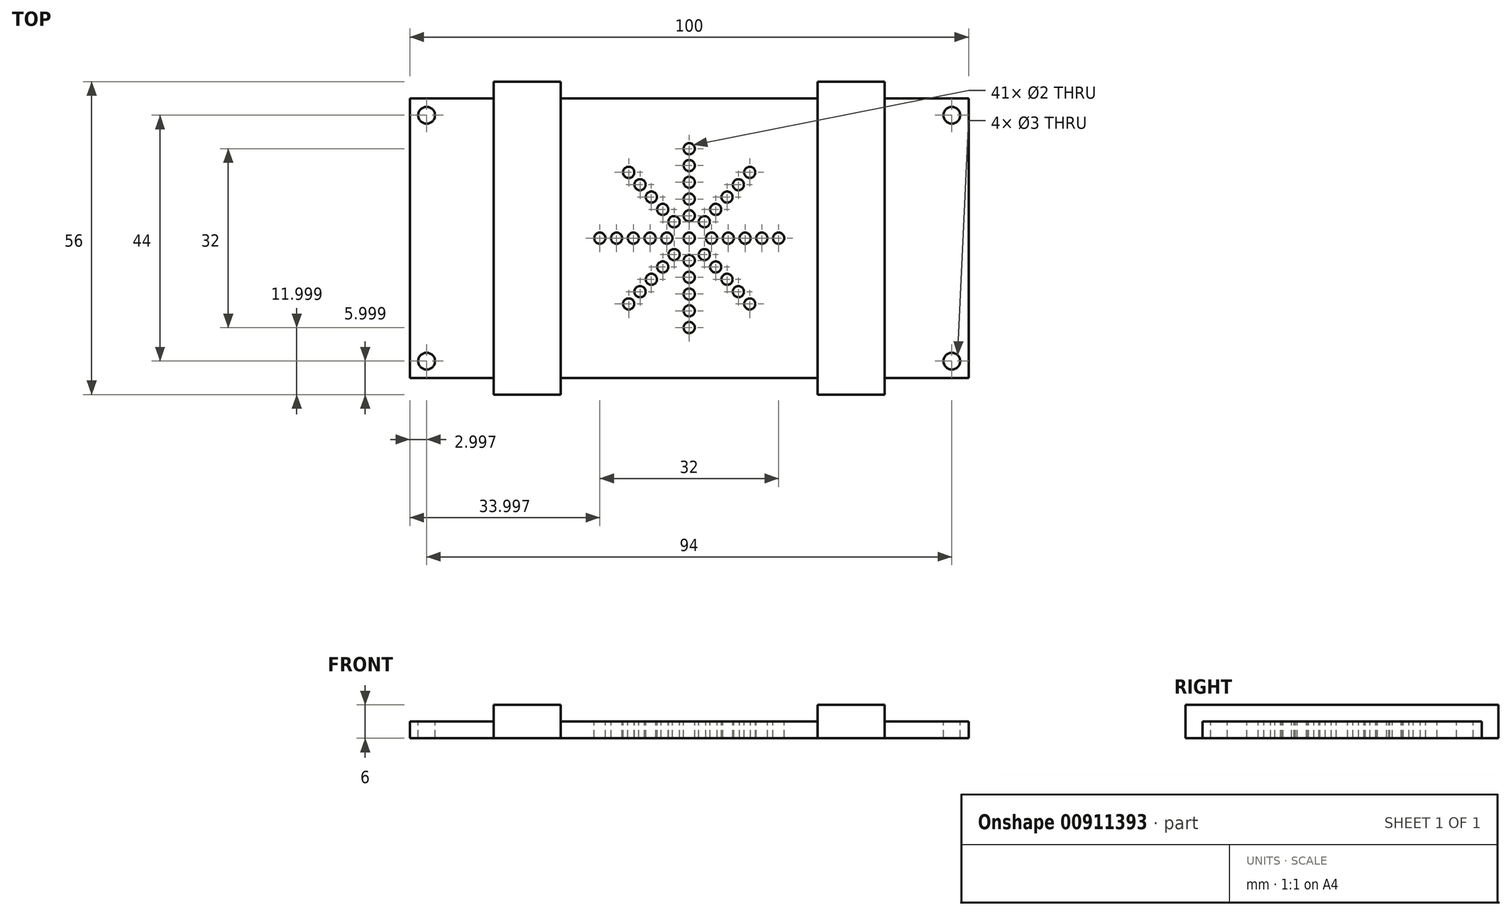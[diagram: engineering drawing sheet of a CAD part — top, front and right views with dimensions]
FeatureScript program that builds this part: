
annotation { "Feature Type Name" : "Feature", "Feature Type Description" : "" }
export const myFeature = defineFeature(function(context is Context, id is Id, definition is map)
    precondition{}
    {
        {
            var Q0;
            Q0=qCreatedBy(makeId("Top.planeOp"),FACE);
            var sketch = newSketch(context, id + "F0", { "sketchPlane" : qUnion([Q0])});
            skLineSegment(sketch, "E0.bottom", {"start": v(-93.13, 32.3) * mm, "end": v(-78.13, 32.3) * mm});
            skLineSegment(sketch, "E0.top", {"start": v(-93.13, -17.7) * mm, "end": v(-78.13, -17.7) * mm});
            skLineSegment(sketch, "E0.left", {"start": v(-93.13, 32.3) * mm, "end": v(-93.13, -17.7) * mm});
            skLineSegment(sketch, "E0.right", {"start": v(6.87, 32.3) * mm, "end": v(6.87, -17.7) * mm});
            skLineSegment(sketch, "E1.top", {"start": v(-78.13, -20.7) * mm, "end": v(-66.13, -20.7) * mm});
            skLineSegment(sketch, "E1.left", {"start": v(-78.13, -17.7) * mm, "end": v(-78.13, -20.7) * mm});
            skLineSegment(sketch, "E1.right", {"start": v(-66.13, -17.7) * mm, "end": v(-66.13, -20.7) * mm});
            skLineSegment(sketch, "E2.top", {"start": v(-20.13, -20.7) * mm, "end": v(-8.13, -20.7) * mm});
            skLineSegment(sketch, "E2.left", {"start": v(-20.13, -17.7) * mm, "end": v(-20.13, -20.7) * mm});
            skLineSegment(sketch, "E2.right", {"start": v(-8.13, -17.7) * mm, "end": v(-8.13, -20.7) * mm});
            skLineSegment(sketch, "E3.top", {"start": v(-78.13, 35.3) * mm, "end": v(-66.13, 35.3) * mm});
            skLineSegment(sketch, "E3.left", {"start": v(-78.13, 32.3) * mm, "end": v(-78.13, 35.3) * mm});
            skLineSegment(sketch, "E3.right", {"start": v(-66.13, 32.3) * mm, "end": v(-66.13, 35.3) * mm});
            skPoint(sketch, "E4.top.end.orphan", {"position": v(-27.6, 35.3) * mm});
            skLineSegment(sketch, "E5.top", {"start": v(-20.13, 35.3) * mm, "end": v(-8.13, 35.3) * mm});
            skLineSegment(sketch, "E5.left", {"start": v(-20.13, 32.3) * mm, "end": v(-20.13, 35.3) * mm});
            skLineSegment(sketch, "E5.right", {"start": v(-8.13, 32.3) * mm, "end": v(-8.13, 35.3) * mm});
            skLineSegment(sketch, "E6.trimOffspring", {"start": v(-66.13, 32.3) * mm, "end": v(-20.13, 32.3) * mm});
            skLineSegment(sketch, "E7.trimOffspring", {"start": v(-8.13, 32.3) * mm, "end": v(6.87, 32.3) * mm});
            skLineSegment(sketch, "E8.trimOffspring", {"start": v(-66.13, -17.7) * mm, "end": v(-20.13, -17.7) * mm});
            skLineSegment(sketch, "E9.trimOffspring", {"start": v(-8.13, -17.7) * mm, "end": v(6.87, -17.7) * mm});
            skSolve(sketch);
        }
        {
            var Q0;
            Q0 = qSketchRegion(id + "F0", true);
            extrude(context, id + "F1", {"entities" : qUnion([Q0]), "depth" : 3 * mm, "offsetDistance" : 25 * mm});
        }
        {
            var Q0;
            Q0=makeQuery(id+"F1.opExtrude","CAP_FACE",FACE,{"disambiguationData":[OSD([sQuery(id+"F0.wireOp",EDGE,"E0.bottom"),sQuery(id+"F0.wireOp",EDGE,"E0.top"),sQuery(id+"F0.wireOp",EDGE,"E0.left"),sQuery(id+"F0.wireOp",EDGE,"E0.right"),sQuery(id+"F0.wireOp",EDGE,"E1.top"),sQuery(id+"F0.wireOp",EDGE,"E1.left"),sQuery(id+"F0.wireOp",EDGE,"E1.right"),sQuery(id+"F0.wireOp",EDGE,"E2.top"),sQuery(id+"F0.wireOp",EDGE,"E2.left"),sQuery(id+"F0.wireOp",EDGE,"E2.right"),sQuery(id+"F0.wireOp",EDGE,"E3.top"),sQuery(id+"F0.wireOp",EDGE,"E3.left"),sQuery(id+"F0.wireOp",EDGE,"E3.right"),sQuery(id+"F0.wireOp",EDGE,"E5.top"),sQuery(id+"F0.wireOp",EDGE,"E5.left"),sQuery(id+"F0.wireOp",EDGE,"E5.right"),sQuery(id+"F0.wireOp",EDGE,"E6.trimOffspring"),sQuery(id+"F0.wireOp",EDGE,"E7.trimOffspring"),sQuery(id+"F0.wireOp",EDGE,"E8.trimOffspring"),sQuery(id+"F0.wireOp",EDGE,"E9.trimOffspring")])],"isStart":false});
            var sketch = newSketch(context, id + "F2", { "sketchPlane" : qUnion([Q0])});
            skPoint(sketch, "E10", {"position": v(-90.13, 29.3) * mm});
            skPoint(sketch, "E11", {"position": v(3.87, -14.7) * mm});
            skPoint(sketch, "E12", {"position": v(-90.13, -14.7) * mm});
            skPoint(sketch, "E13", {"position": v(3.87, 29.3) * mm});
            skLineSegment(sketch, "E14", {"start": v(-78.13, 32.3) * mm, "end": v(-78.13, -17.7) * mm});
            skLineSegment(sketch, "E15", {"start": v(-78.13, -17.7) * mm, "end": v(-78.13, -20.7) * mm});
            skLineSegment(sketch, "E16", {"start": v(-78.13, -20.7) * mm, "end": v(-66.13, -20.7) * mm});
            skLineSegment(sketch, "E17", {"start": v(-66.13, -20.7) * mm, "end": v(-66.13, -17.7) * mm});
            skLineSegment(sketch, "E18", {"start": v(-66.13, -17.7) * mm, "end": v(-66.13, 35.3) * mm});
            skLineSegment(sketch, "E19", {"start": v(-66.13, 35.3) * mm, "end": v(-78.13, 35.3) * mm});
            skLineSegment(sketch, "E20", {"start": v(-78.13, 35.3) * mm, "end": v(-78.13, 32.3) * mm});
            skLineSegment(sketch, "E21", {"start": v(-20.13, 35.3) * mm, "end": v(-20.13, -20.7) * mm});
            skLineSegment(sketch, "E22", {"start": v(-20.13, -20.7) * mm, "end": v(-8.13, -20.7) * mm});
            skLineSegment(sketch, "E23", {"start": v(-8.13, -20.7) * mm, "end": v(-8.13, 35.3) * mm});
            skLineSegment(sketch, "E24", {"start": v(-8.13, 35.3) * mm, "end": v(-20.13, 35.3) * mm});
            skSolve(sketch);
        }
        {
            var Q0;
            Q0 = qSketchRegion(id + "F2", true);
            extrude(context, id + "F3", {"entities" : qUnion([Q0]), "operationType" : NewBodyOperationType.ADD, "depth" : 3 * mm, "offsetDistance" : 25 * mm});
        }
        {
            var Q0;
            Q0=sQuery(id+"F2.wireOp",VERTEX,"E12");
            var Q1;
            Q1=sQuery(id+"F2.wireOp",VERTEX,"E10");
            var Q2;
            Q2=sQuery(id+"F2.wireOp",VERTEX,"E11");
            var Q3;
            Q3=sQuery(id+"F2.wireOp",VERTEX,"E13");
            var Q4;
            Q4=makeQuery(id+"F1.opExtrude","SWEPT_BODY",BODY,{"disambiguationData":[OSD([sQuery(id+"F0.wireOp",EDGE,"E0.bottom"),sQuery(id+"F0.wireOp",EDGE,"E0.top"),sQuery(id+"F0.wireOp",EDGE,"E0.left"),sQuery(id+"F0.wireOp",EDGE,"E0.right"),sQuery(id+"F0.wireOp",EDGE,"E1.top"),sQuery(id+"F0.wireOp",EDGE,"E1.left"),sQuery(id+"F0.wireOp",EDGE,"E1.right"),sQuery(id+"F0.wireOp",EDGE,"E2.top"),sQuery(id+"F0.wireOp",EDGE,"E2.left"),sQuery(id+"F0.wireOp",EDGE,"E2.right"),sQuery(id+"F0.wireOp",EDGE,"E3.top"),sQuery(id+"F0.wireOp",EDGE,"E3.left"),sQuery(id+"F0.wireOp",EDGE,"E3.right"),sQuery(id+"F0.wireOp",EDGE,"E5.top"),sQuery(id+"F0.wireOp",EDGE,"E5.left"),sQuery(id+"F0.wireOp",EDGE,"E5.right"),sQuery(id+"F0.wireOp",EDGE,"E6.trimOffspring"),sQuery(id+"F0.wireOp",EDGE,"E7.trimOffspring"),sQuery(id+"F0.wireOp",EDGE,"E8.trimOffspring"),sQuery(id+"F0.wireOp",EDGE,"E9.trimOffspring")])]});
            hole(context, id + "F4", {"style" : HoleStyle.SIMPLE, "endStyle" : HoleEndStyle.THROUGH, "holeDiameter" : 3 * mm, "majorDiameter" : 5 * mm, "isTappedThrough" : true, "tappedDepth" : 12 * mm, "tapClearance" : 3, "locations" : qUnion([Q0, Q1, Q2, Q3]), "scope" : qUnion([Q4])});
        }
        {
            var Q0;
            {var subQ0=sQuery(id+"F0.wireOp",EDGE,"E5.left");var subQ1=sQuery(id+"F0.wireOp",EDGE,"E3.right");var subQ2=sQuery(id+"F0.wireOp",EDGE,"E2.left");var subQ3=sQuery(id+"F0.wireOp",EDGE,"E1.right");var subQ4=sQuery(id+"F0.wireOp",EDGE,"E6.trimOffspring");var subQ5=sQuery(id+"F0.wireOp",EDGE,"E8.trimOffspring");Q0=makeQuery(id+"F3.boolean.opBoolean","SPLIT",FACE,{"disambiguationData":[TD([makeQuery(id+"F1.opExtrude","SWEPT_FACE",FACE,{"disambiguationData":[OSD([subQ3])]})])],"derivedFrom":makeQuery(id+"F1.opExtrude","CAP_FACE",FACE,{"disambiguationData":[OSD([sQuery(id+"F0.wireOp",EDGE,"E0.bottom"),sQuery(id+"F0.wireOp",EDGE,"E0.top"),sQuery(id+"F0.wireOp",EDGE,"E0.left"),sQuery(id+"F0.wireOp",EDGE,"E0.right"),sQuery(id+"F0.wireOp",EDGE,"E1.top"),sQuery(id+"F0.wireOp",EDGE,"E1.left"),subQ3,sQuery(id+"F0.wireOp",EDGE,"E2.top"),subQ2,sQuery(id+"F0.wireOp",EDGE,"E2.right"),sQuery(id+"F0.wireOp",EDGE,"E3.top"),sQuery(id+"F0.wireOp",EDGE,"E3.left"),subQ1,sQuery(id+"F0.wireOp",EDGE,"E5.top"),subQ0,sQuery(id+"F0.wireOp",EDGE,"E5.right"),subQ4,sQuery(id+"F0.wireOp",EDGE,"E7.trimOffspring"),subQ5,sQuery(id+"F0.wireOp",EDGE,"E9.trimOffspring")])],"isStart":false})});}
            var sketch = newSketch(context, id + "F5", { "sketchPlane" : qUnion([Q0])});
            skLineSegment(sketch, "E25", {"start": v(-43.13, -17.7) * mm, "end": v(-43.13, 32.3) * mm});
            skLineSegment(sketch, "E26", {"start": v(-66.13, 7.3) * mm, "end": v(-20.13, 7.3) * mm});
            skCircle(sketch, "E27", {"center": v(-43.13, 7.3) * mm, "radius": 4 * mm});
            skCircle(sketch, "E28", {"center": v(-43.13, 7.3) * mm, "radius": 7 * mm});
            skCircle(sketch, "E29", {"center": v(-43.13, 7.3) * mm, "radius": 10 * mm});
            skCircle(sketch, "E30", {"center": v(-43.13, 7.3) * mm, "radius": 13 * mm});
            skCircle(sketch, "E31", {"center": v(-43.13, 7.3) * mm, "radius": 16 * mm});
            skLineSegment(sketch, "E32", {"start": v(-66.13, 32.3) * mm, "end": v(-20.13, -17.7) * mm});
            skLineSegment(sketch, "E33", {"start": v(-66.13, -17.7) * mm, "end": v(-20.13, 32.3) * mm});
            skPoint(sketch, "E34", {"position": v(-43.13, 0.3) * mm});
            skPoint(sketch, "E35", {"position": v(-38.4, 2.15) * mm});
            skPoint(sketch, "E36", {"position": v(-36.13, 7.3) * mm});
            skPoint(sketch, "E37", {"position": v(-47.87, 2.15) * mm});
            skPoint(sketch, "E38", {"position": v(-50.13, 7.3) * mm});
            skPoint(sketch, "E39", {"position": v(-47.87, 12.45) * mm});
            skPoint(sketch, "E40", {"position": v(-40.43, 4.36) * mm});
            skPoint(sketch, "E41", {"position": v(-43.13, 3.3) * mm});
            skPoint(sketch, "E42", {"position": v(-45.84, 4.36) * mm});
            skPoint(sketch, "E43", {"position": v(-47.13, 7.3) * mm});
            skPoint(sketch, "E44", {"position": v(-45.84, 10.24) * mm});
            skPoint(sketch, "E45", {"position": v(-43.13, 11.3) * mm});
            skPoint(sketch, "E46", {"position": v(-40.43, 10.24) * mm});
            skPoint(sketch, "E47", {"position": v(-38.4, 12.45) * mm});
            skPoint(sketch, "E48", {"position": v(-43.13, 14.3) * mm});
            skPoint(sketch, "E49", {"position": v(-43.13, 17.3) * mm});
            skPoint(sketch, "E50", {"position": v(-50.27, 14.3) * mm});
            skPoint(sketch, "E51", {"position": v(-53.13, 7.3) * mm});
            skPoint(sketch, "E52", {"position": v(-43.13, -2.7) * mm});
            skPoint(sketch, "E53", {"position": v(-43.13, -5.7) * mm});
            skPoint(sketch, "E54", {"position": v(-43.13, -8.7) * mm});
            skPoint(sketch, "E55", {"position": v(-32.3, -4.48) * mm});
            skPoint(sketch, "E56", {"position": v(-33.13, 7.3) * mm});
            skPoint(sketch, "E57", {"position": v(-30.13, 7.3) * mm});
            skPoint(sketch, "E58", {"position": v(-27.13, 7.3) * mm});
            skPoint(sketch, "E59", {"position": v(-36, 14.3) * mm});
            skPoint(sketch, "E60", {"position": v(-34.83, 17.3) * mm});
            skPoint(sketch, "E61", {"position": v(-32.3, 19.07) * mm});
            skPoint(sketch, "E62", {"position": v(-43.13, 23.3) * mm});
            skPoint(sketch, "E63", {"position": v(-43.13, 20.3) * mm});
            skPoint(sketch, "E64", {"position": v(-51.94, 16.87) * mm});
            skPoint(sketch, "E65", {"position": v(-53.97, 19.07) * mm});
            skPoint(sketch, "E66", {"position": v(-59.13, 7.3) * mm});
            skPoint(sketch, "E67", {"position": v(-56.13, 7.3) * mm});
            skPoint(sketch, "E68", {"position": v(-51.94, -2.27) * mm});
            skPoint(sketch, "E69", {"position": v(-53.97, -4.48) * mm});
            skPoint(sketch, "E70", {"position": v(-34.33, -2.27) * mm});
            skPoint(sketch, "E71", {"position": v(-36.36, -0.06) * mm});
            skPoint(sketch, "E72", {"position": v(-39.13, 7.3) * mm});
            skPoint(sketch, "E73", {"position": v(-36.36, 14.66) * mm});
            skPoint(sketch, "E74", {"position": v(-34.33, 16.87) * mm});
            skPoint(sketch, "E75", {"position": v(-49.9, -0.06) * mm});
            skPoint(sketch, "E76", {"position": v(-49.9, 14.66) * mm});
            skSolve(sketch);
        }
        {
            var Q0;
            Q0=sQuery(id+"F5.wireOp",VERTEX,"E65");
            var Q1;
            Q1=sQuery(id+"F5.wireOp",VERTEX,"E62");
            var Q2;
            Q2=sQuery(id+"F5.wireOp",VERTEX,"E61");
            var Q3;
            Q3=sQuery(id+"F5.wireOp",VERTEX,"E58");
            var Q4;
            Q4=sQuery(id+"F5.wireOp",VERTEX,"E55");
            var Q5;
            Q5=sQuery(id+"F5.wireOp",VERTEX,"E70");
            var Q6;
            Q6=sQuery(id+"F5.wireOp",VERTEX,"E71");
            var Q7;
            Q7=sQuery(id+"F5.wireOp",VERTEX,"E35");
            var Q8;
            Q8=sQuery(id+"F5.wireOp",VERTEX,"E40");
            var Q9;
            Q9=sQuery(id+"F5.wireOp",VERTEX,"E72");
            var Q10;
            Q10=sQuery(id+"F5.wireOp",VERTEX,"E36");
            var Q11;
            Q11=sQuery(id+"F5.wireOp",VERTEX,"E56");
            var Q12;
            Q12=sQuery(id+"F5.wireOp",VERTEX,"E57");
            var Q13;
            Q13=sQuery(id+"F5.wireOp",VERTEX,"E46");
            var Q14;
            Q14=sQuery(id+"F5.wireOp",VERTEX,"E47");
            var Q15;
            Q15=sQuery(id+"F5.wireOp",VERTEX,"E73");
            var Q16;
            Q16=sQuery(id+"F5.wireOp",VERTEX,"E74");
            var Q17;
            Q17=sQuery(id+"F5.wireOp",VERTEX,"E45");
            var Q18;
            Q18=sQuery(id+"F5.wireOp",VERTEX,"E48");
            var Q19;
            Q19=sQuery(id+"F5.wireOp",VERTEX,"E49");
            var Q20;
            Q20=sQuery(id+"F5.wireOp",VERTEX,"E63");
            var Q21;
            Q21=sQuery(id+"F5.wireOp",VERTEX,"E64");
            var Q22;
            Q22=sQuery(id+"F5.wireOp",VERTEX,"E76");
            var Q23;
            Q23=sQuery(id+"F5.wireOp",VERTEX,"E39");
            var Q24;
            Q24=sQuery(id+"F5.wireOp",VERTEX,"E44");
            var Q25;
            Q25=sQuery(id+"F5.wireOp",VERTEX,"E43");
            var Q26;
            Q26=sQuery(id+"F5.wireOp",VERTEX,"E42");
            var Q27;
            Q27=sQuery(id+"F5.wireOp",VERTEX,"E41");
            var Q28;
            Q28=sQuery(id+"F5.wireOp",VERTEX,"E34");
            var Q29;
            Q29=sQuery(id+"F5.wireOp",VERTEX,"E52");
            var Q30;
            Q30=sQuery(id+"F5.wireOp",VERTEX,"E53");
            var Q31;
            Q31=sQuery(id+"F5.wireOp",VERTEX,"E54");
            var Q32;
            Q32=sQuery(id+"F5.wireOp",VERTEX,"E69");
            var Q33;
            Q33=sQuery(id+"F5.wireOp",VERTEX,"E68");
            var Q34;
            Q34=sQuery(id+"F5.wireOp",VERTEX,"E75");
            var Q35;
            Q35=sQuery(id+"F5.wireOp",VERTEX,"E37");
            var Q36;
            Q36=sQuery(id+"F5.wireOp",VERTEX,"E38");
            var Q37;
            Q37=sQuery(id+"F5.wireOp",VERTEX,"E51");
            var Q38;
            Q38=sQuery(id+"F5.wireOp",VERTEX,"E67");
            var Q39;
            Q39=sQuery(id+"F5.wireOp",VERTEX,"E66");
            var Q40;
            Q40=sQuery(id+"F5.wireOp",VERTEX,"E27.center");
            var Q41;
            Q41=makeQuery(id+"F1.opExtrude","SWEPT_BODY",BODY,{"disambiguationData":[OSD([sQuery(id+"F0.wireOp",EDGE,"E0.bottom"),sQuery(id+"F0.wireOp",EDGE,"E0.top"),sQuery(id+"F0.wireOp",EDGE,"E0.left"),sQuery(id+"F0.wireOp",EDGE,"E0.right"),sQuery(id+"F0.wireOp",EDGE,"E1.top"),sQuery(id+"F0.wireOp",EDGE,"E1.left"),sQuery(id+"F0.wireOp",EDGE,"E1.right"),sQuery(id+"F0.wireOp",EDGE,"E2.top"),sQuery(id+"F0.wireOp",EDGE,"E2.left"),sQuery(id+"F0.wireOp",EDGE,"E2.right"),sQuery(id+"F0.wireOp",EDGE,"E3.top"),sQuery(id+"F0.wireOp",EDGE,"E3.left"),sQuery(id+"F0.wireOp",EDGE,"E3.right"),sQuery(id+"F0.wireOp",EDGE,"E5.top"),sQuery(id+"F0.wireOp",EDGE,"E5.left"),sQuery(id+"F0.wireOp",EDGE,"E5.right"),sQuery(id+"F0.wireOp",EDGE,"E6.trimOffspring"),sQuery(id+"F0.wireOp",EDGE,"E7.trimOffspring"),sQuery(id+"F0.wireOp",EDGE,"E8.trimOffspring"),sQuery(id+"F0.wireOp",EDGE,"E9.trimOffspring")])]});
            hole(context, id + "F6", {"style" : HoleStyle.SIMPLE, "endStyle" : HoleEndStyle.THROUGH, "holeDiameter" : 2 * mm, "majorDiameter" : 5 * mm, "isTappedThrough" : true, "tappedDepth" : 12 * mm, "tapClearance" : 3, "locations" : qUnion([Q0, Q1, Q2, Q3, Q4, Q5, Q6, Q7, Q8, Q9, Q10, Q11, Q12, Q13, Q14, Q15, Q16, Q17, Q18, Q19, Q20, Q21, Q22, Q23, Q24, Q25, Q26, Q27, Q28, Q29, Q30, Q31, Q32, Q33, Q34, Q35, Q36, Q37, Q38, Q39, Q40]), "scope" : qUnion([Q41])});
        }
    });
